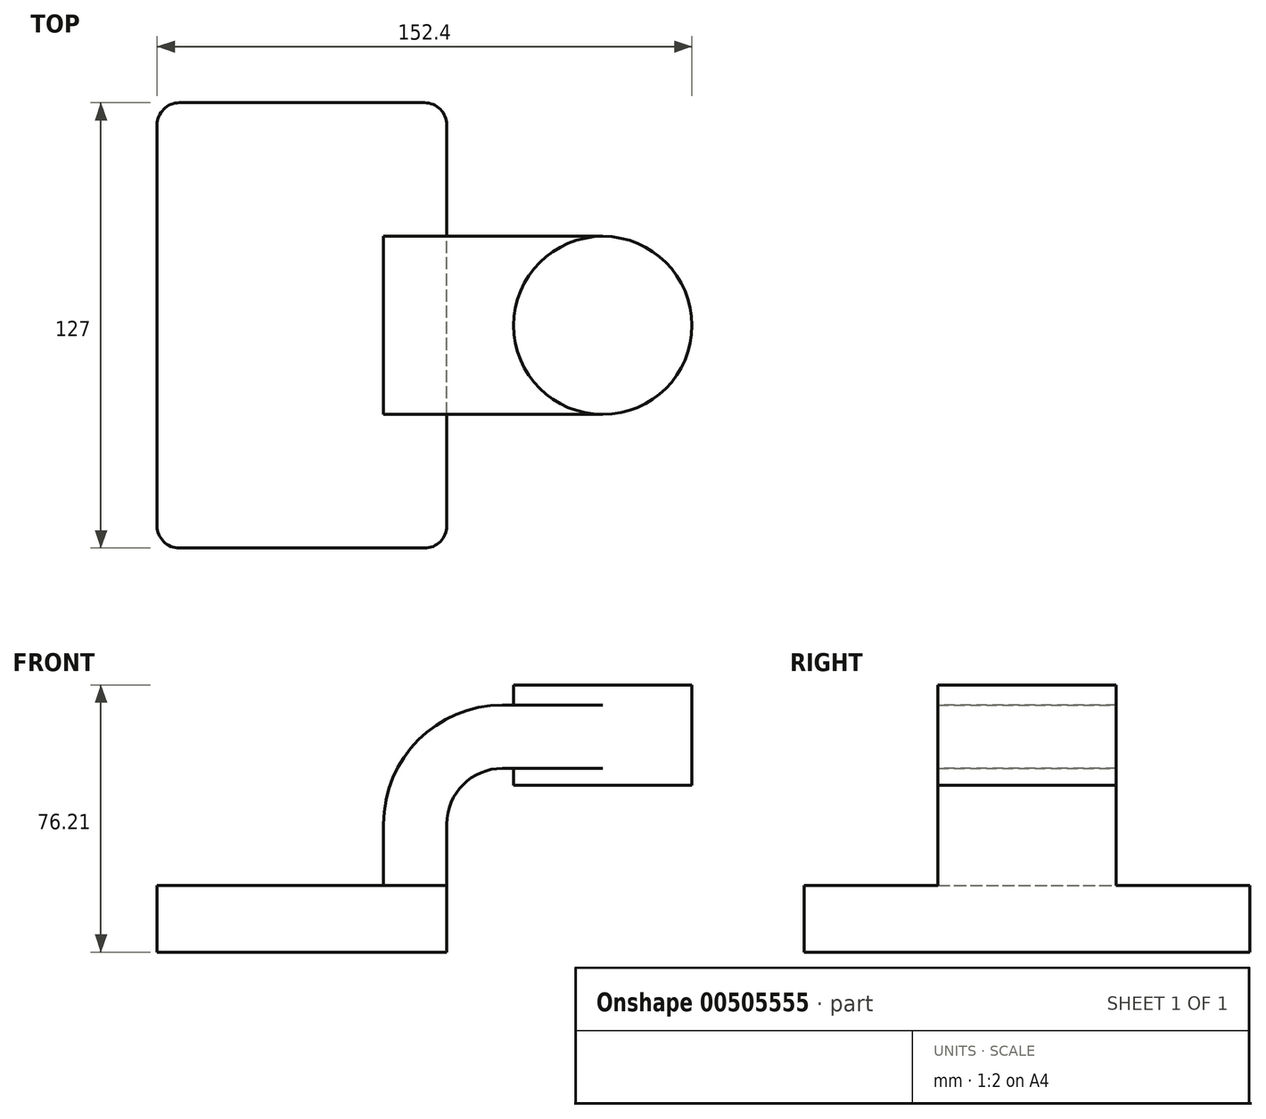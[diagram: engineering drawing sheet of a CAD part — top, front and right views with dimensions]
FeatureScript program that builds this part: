
annotation { "Feature Type Name" : "Feature", "Feature Type Description" : "" }
export const myFeature = defineFeature(function(context is Context, id is Id, definition is map)
    precondition{}
    {
        {
            var Q0;
            Q0=qCreatedBy(makeId("Front.planeOp"),FACE);
            var sketch = newSketch(context, id + "F0", { "sketchPlane" : qUnion([Q0])});
            skLineSegment(sketch, "E0.bottom", {"start": v(-41.28, -9.53) * mm, "end": v(41.28, -9.53) * mm});
            skLineSegment(sketch, "E0.top", {"start": v(-41.28, 9.52) * mm, "end": v(41.28, 9.52) * mm});
            skLineSegment(sketch, "E0.left", {"start": v(-41.28, -9.53) * mm, "end": v(-41.28, 9.52) * mm});
            skLineSegment(sketch, "E0.right", {"start": v(41.28, -9.53) * mm, "end": v(41.28, 9.52) * mm});
            skPoint(sketch, "E0.middle", {"position": v(0, 0) * mm});
            skLineSegment(sketch, "E1.bottom", {"start": v(60.32, 38.1) * mm, "end": v(111.12, 38.1) * mm});
            skLineSegment(sketch, "E1.top", {"start": v(60.32, 66.67) * mm, "end": v(111.12, 66.67) * mm});
            skLineSegment(sketch, "E1.left", {"start": v(60.32, 38.1) * mm, "end": v(60.32, 66.67) * mm});
            skLineSegment(sketch, "E1.right", {"start": v(111.12, 38.1) * mm, "end": v(111.12, 66.67) * mm});
            skPoint(sketch, "E1.middle", {"position": v(85.72, 52.39) * mm});
            skLineSegment(sketch, "E2", {"start": v(41.28, 9.52) * mm, "end": v(41.28, 27) * mm});
            skArc(sketch, "E3", {"start": v(41.27, 27) * mm, "mid": v(45.92, 38.23) * mm, "end": v(57.15, 42.88) * mm});
            skLineSegment(sketch, "E4", {"start": v(57.15, 42.88) * mm, "end": v(85.72, 42.88) * mm});
            skLineSegment(sketch, "E5.0", {"start": v(57.15, 60.9) * mm, "end": v(85.87, 60.9) * mm});
            skArc(sketch, "E5.1", {"start": v(23.24, 27) * mm, "mid": v(33.17, 50.98) * mm, "end": v(57.15, 60.9) * mm});
            skLineSegment(sketch, "E5.2", {"start": v(23.24, 9.52) * mm, "end": v(23.24, 27) * mm});
            skFitSpline(sketch, "E6", {"points": [v(-41.28, 9.53) * mm, v(57.15, 60.9) * mm], "startDerivative": vector(21.1, 110.77) * mm, "endDerivative": vector(141.02, -5.75) * mm});
            skLineSegment(sketch, "E7", {"start": v(85.72, 66.67) * mm, "end": v(85.72, 38.1) * mm});
            skSolve(sketch);
        }
        {
            var Q0;
            Q0=makeQuery(id+"F0.imprint","IMPRINT",FACE,{"disambiguationData":[TD([[makeQuery(id+"F0.imprint","IMPRINT",EDGE,{"derivedFrom":sQuery(id+"F0.wireOp",EDGE,"E0.bottom")}),1.0]])]});
            extrude(context, id + "F1", {"entities" : qUnion([Q0]), "endBound" : BoundingType.SYMMETRIC, "depth" : 127 * mm});
        }
        {
            var Q0;
            {var subQ1=sQuery(id+"F0.wireOp",EDGE,"E2");Q0=makeQuery(id+"F0.imprint","IMPRINT",FACE,{"disambiguationData":[TD([[makeQuery(id+"F0.imprint","IMPRINT",EDGE,{"derivedFrom":subQ1}),1.0]])]});}
            var Q1;
            {var subQ0=sQuery(id+"F0.wireOp",EDGE,"E4");var subQ1=sQuery(id+"F0.wireOp",EDGE,"E1.left");var subQ2=makeQuery(id+"F0.imprint","INTERSECT",VERTEX,{"derivedFrom":[subQ1,subQ0]});Q1=makeQuery(id+"F0.imprint","IMPRINT",FACE,{"disambiguationData":[TD([[makeQuery(id+"F0.imprint","IMPRINT",EDGE,{"disambiguationData":[TD([[subQ2,-1.0]])],"derivedFrom":subQ1}),-1.0]])]});}
            extrude(context, id + "F2", {"entities" : qUnion([Q0, Q1]), "operationType" : NewBodyOperationType.ADD, "endBound" : BoundingType.SYMMETRIC, "depth" : 50.8 * mm});
        }
        {
            var Q0;
            Q0=makeQuery(id+"F0.imprint","IMPRINT",FACE,{"disambiguationData":[TD([[makeQuery(id+"F0.imprint","IMPRINT",EDGE,{"derivedFrom":sQuery(id+"F0.wireOp",EDGE,"E5.1")}),1.0]])]});
            extrude(context, id + "F3", {"entities" : qUnion([Q0]), "operationType" : NewBodyOperationType.ADD, "endBound" : BoundingType.SYMMETRIC, "depth" : 12.7 * mm});
        }
        {
            var Q0;
            {var subQ4=sQuery(id+"F0.wireOp",EDGE,"E1.right");Q0=makeQuery(id+"F0.imprint","IMPRINT",FACE,{"disambiguationData":[TD([[makeQuery(id+"F0.imprint","IMPRINT",EDGE,{"derivedFrom":subQ4}),1.0]])]});}
            var Q1;
            {var subQ4=sQuery(id+"F0.wireOp",EDGE,"E1.right");Q1=makeQuery(id+"F0.imprint","IMPRINT",FACE,{"disambiguationData":[TD([[makeQuery(id+"F0.imprint","IMPRINT",EDGE,{"derivedFrom":subQ4}),1.0]])]});}
            var Q2;
            Q2=sQuery(id+"F0.wireOp",EDGE,"E7");
            revolve(context, id + "F4", {"operationType" : NewBodyOperationType.ADD, "entities" : qUnion([Q0, Q1]), "axis" : qUnion([Q2]), "revolveType" : RevolveType.FULL});
        }
        {
            var Q0;
            Q0=makeQuery(id+"F1.opExtrude","CAP_EDGE",EDGE,{"disambiguationData":[OSD([sQuery(id+"F0.wireOp",EDGE,"E0.left")])],"isStart":false});
            var Q1;
            Q1=makeQuery(id+"F1.opExtrude","CAP_EDGE",EDGE,{"disambiguationData":[OSD([sQuery(id+"F0.wireOp",EDGE,"E0.right")])],"isStart":false});
            var Q2;
            Q2=makeQuery(id+"F1.opExtrude","CAP_EDGE",EDGE,{"disambiguationData":[OSD([sQuery(id+"F0.wireOp",EDGE,"E0.left")])],"isStart":true});
            var Q3;
            Q3=makeQuery(id+"F1.opExtrude","CAP_EDGE",EDGE,{"disambiguationData":[OSD([sQuery(id+"F0.wireOp",EDGE,"E0.right")])],"isStart":true});
            fillet(context, id + "F5", {"entities" : qUnion([Q0, Q1, Q2, Q3]), "radius" : 6.35 * mm, "tangentPropagation" : true, "allowEdgeOverflow" : false});
        }
    });
